# Revit family: L450xH438_GRYFIT VX-6V, Smoke damper
name_source: partatom
category: Duct Accessories
units: mm (PartAtom-declared; Revit-internal decimal feet)

## family parameters
Always vertical = Yes
Cut with Voids When Loaded = No
OmniClass Number = 23.75.70.11.14.14
OmniClass Title = Dampers for Air Ductwork
Part Type = Damper
Round Connector Dimension = Use Diameter
Shared = No
Work Plane-Based = No

## types (1)
- GRYFIT VX-6V (1H,1V), LxH=450x438 + LDG-24 + EI24 + 1WKKP + GPV-M + RM, LxH=450x438
    Actuator type. = LDG
    Actuator voltage. = 24/48 V AC/DC
    Colour of ext. grille. = natural
    Damper Length = 150 mm
    Damper Material = <By Category>
    Damper mounting frame (RM) = Yes
    Damper opening direction. = right
    Double Beginning and End (2WKKP) = Beginning and End (1WKKP)
    Electromagnet = Yes
    Electromagnet type. = impulse
    Electromagnet voltage. = 24/48 V DC
    External grille assembly. = screws
    External louvre. = GPV-M
    Fire resistance class. = EI 60 (ved i↔o) S 1500Pa AA multi
    Geometry = GRYFIT VX-6V (1H,1V), LxH=450x438 + LDG-24 + EI24 + 1WKKP + GPV-M + RM, LxH=450x438
    Half Damper Length = 75 mm
    Height (H). = 438
    Height (Hge). = 517
    Height (Hht). = 491
    Height (Hl). = 382
    Height (Hr). = 458
    Length (P). = 510
    Material of ext. grille. = Galvanized steel
    Material. = Galvanized steel
    Protection grille. = Yes
    Type. = VX-6-V, EI60S, 1V + LDG
    Width (L). = 450
    Width (Lge). = 519
    Width (Lht). = 498
    Width (Ll). = 384
    Width (Lr). = 470
    anglXY1 = 0.00°
    anglZ1 = 0.00°
    heightcon1 = 438 mm
    lengX1 = 53 mm
    lengXY1 = 600 mm  [stored 1.9685 ft]
    lengXYZ1 = 500 mm  [stored 1.64042 ft]
    lengY1 = 0 mm  [stored 0 ft]
    lengZ1 = 0 mm  [stored 0 ft]
    rotcon1 = 0 mm
    widthcon1 = 450 mm

note: [stored X ft] marks values corroborated as IEEE doubles in the binary element streams (Revit-internal decimal feet)

## geometry (parser evidence)
native form markers: Sweep x2
no freeform markers — native parametric forms only
